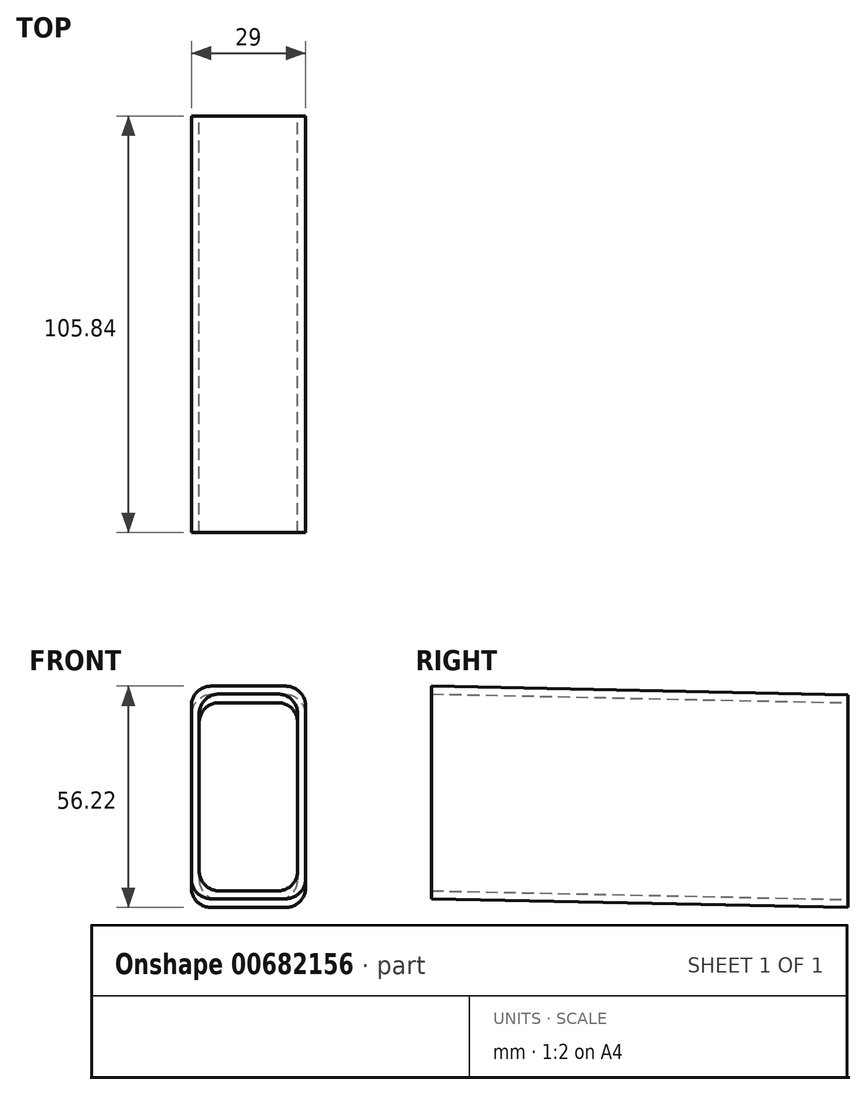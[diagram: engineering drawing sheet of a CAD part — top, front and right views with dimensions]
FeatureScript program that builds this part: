
annotation { "Feature Type Name" : "Feature", "Feature Type Description" : "" }
export const myFeature = defineFeature(function(context is Context, id is Id, definition is map)
    precondition{}
    {
        {
            var Q0;
            Q0=qCreatedBy(makeId("Front.planeOp"),FACE);
            var sketch = newSketch(context, id + "F0", { "sketchPlane" : qUnion([Q0])});
            skSolve(sketch);
        }
        {
            var Q0;
            Q0=qCreatedBy(makeId("Front.planeOp"),FACE);
            var sketch = newSketch(context, id + "F1", { "sketchPlane" : qUnion([Q0])});
            skLineSegment(sketch, "E0.bottom", {"start": v(12.5, 25) * mm, "end": v(-12.5, 25) * mm});
            skLineSegment(sketch, "E0.top", {"start": v(12.5, -25) * mm, "end": v(-12.5, -25) * mm});
            skLineSegment(sketch, "E0.left", {"start": v(12.5, 25) * mm, "end": v(12.5, -25) * mm});
            skLineSegment(sketch, "E0.right", {"start": v(-12.5, 25) * mm, "end": v(-12.5, -25) * mm});
            skPoint(sketch, "E0.middle", {"position": v(0, 0) * mm});
            skLineSegment(sketch, "E1.0", {"start": v(-14.5, 27) * mm, "end": v(-14.5, -27) * mm});
            skLineSegment(sketch, "E1.1", {"start": v(14.5, 27) * mm, "end": v(-14.5, 27) * mm});
            skLineSegment(sketch, "E1.2", {"start": v(14.5, 27) * mm, "end": v(14.5, -27) * mm});
            skLineSegment(sketch, "E1.3", {"start": v(14.5, -27) * mm, "end": v(-14.5, -27) * mm});
            skSolve(sketch);
        }
        {
            var Q0;
            Q0=qCreatedBy(makeId("Right.planeOp"),FACE);
            var sketch = newSketch(context, id + "F2", { "sketchPlane" : qUnion([Q0])});
            skLineSegment(sketch, "E2", {"start": v(0, 0) * mm, "end": v(105.84, -2.22) * mm});
            skLineSegment(sketch, "E3", {"start": v(105.84, -2.22) * mm, "end": v(1314.9, -890.02) * mm});
            skSolve(sketch);
        }
        {
            var Q0;
            Q0 = qSketchRegion(id + "F0", true);
            var Q1;
            Q1=makeQuery(id+"F1.imprint","IMPRINT",FACE,{"disambiguationData":[TD([[makeQuery(id+"F1.imprint","IMPRINT",EDGE,{"derivedFrom":sQuery(id+"F1.wireOp",EDGE,"E0.bottom")}),-1.0]])]});
            var Q2;
            Q2=sQuery(id+"F2.wireOp",EDGE,"E2");
            sweep(context, id + "F3", {"profiles" : qUnion([Q0, Q1]), "path" : qUnion([Q2])});
        }
        {
            var Q0;
            Q0=makeQuery(id+"F3.opSweep","SWEPT_EDGE",EDGE,{"disambiguationData":[OSD([sQuery(id+"F1.wireOp",EDGE,"E1.1"),sQuery(id+"F1.wireOp",EDGE,"E1.2"),sQuery(id+"F2.wireOp",EDGE,"E2")])]});
            var Q1;
            Q1=makeQuery(id+"F3.opSweep","SWEPT_EDGE",EDGE,{"disambiguationData":[OSD([sQuery(id+"F1.wireOp",EDGE,"E1.0"),sQuery(id+"F1.wireOp",EDGE,"E1.1"),sQuery(id+"F2.wireOp",EDGE,"E2")])]});
            var Q2;
            Q2=makeQuery(id+"F3.opSweep","SWEPT_EDGE",EDGE,{"disambiguationData":[OSD([sQuery(id+"F1.wireOp",EDGE,"E0.top"),sQuery(id+"F1.wireOp",EDGE,"E0.right"),sQuery(id+"F2.wireOp",EDGE,"E2")])]});
            var Q3;
            Q3=makeQuery(id+"F3.opSweep","SWEPT_EDGE",EDGE,{"disambiguationData":[OSD([sQuery(id+"F1.wireOp",EDGE,"E0.bottom"),sQuery(id+"F1.wireOp",EDGE,"E0.right"),sQuery(id+"F2.wireOp",EDGE,"E2")])]});
            var Q4;
            Q4=makeQuery(id+"F3.opSweep","SWEPT_EDGE",EDGE,{"disambiguationData":[OSD([sQuery(id+"F1.wireOp",EDGE,"E1.0"),sQuery(id+"F1.wireOp",EDGE,"E1.3"),sQuery(id+"F2.wireOp",EDGE,"E2")])]});
            var Q5;
            Q5=makeQuery(id+"F3.opSweep","SWEPT_EDGE",EDGE,{"disambiguationData":[OSD([sQuery(id+"F1.wireOp",EDGE,"E0.bottom"),sQuery(id+"F1.wireOp",EDGE,"E0.left"),sQuery(id+"F2.wireOp",EDGE,"E2")])]});
            var Q6;
            Q6=makeQuery(id+"F3.opSweep","SWEPT_EDGE",EDGE,{"disambiguationData":[OSD([sQuery(id+"F1.wireOp",EDGE,"E1.2"),sQuery(id+"F1.wireOp",EDGE,"E1.3"),sQuery(id+"F2.wireOp",EDGE,"E2")])]});
            var Q7;
            Q7=makeQuery(id+"F3.opSweep","SWEPT_EDGE",EDGE,{"disambiguationData":[OSD([sQuery(id+"F1.wireOp",EDGE,"E0.top"),sQuery(id+"F1.wireOp",EDGE,"E0.left"),sQuery(id+"F2.wireOp",EDGE,"E2")])]});
            fillet(context, id + "F4", {"entities" : qUnion([Q0, Q1, Q2, Q3, Q4, Q5, Q6, Q7]), "radius" : 5 * mm, "tangentPropagation" : true, "allowEdgeOverflow" : false});
        }
    });
